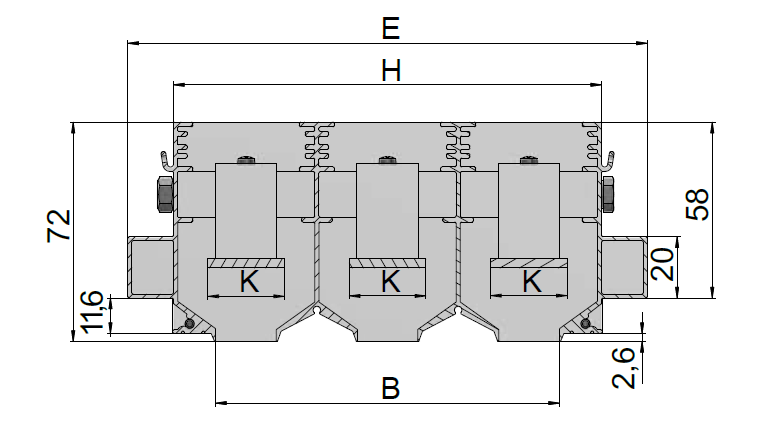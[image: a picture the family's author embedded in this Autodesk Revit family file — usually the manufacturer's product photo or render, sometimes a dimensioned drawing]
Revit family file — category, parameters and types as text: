
# Revit family: GR_Адаптер линейный_Муфта(n)_TL-КСД_R21
name_source: partatom
category: Соединительные детали воздуховодов
units: mm (PartAtom-declared; Revit-internal decimal feet)

## family parameters
Всегда вертикально = Да
Заголовок OmniClass = Metal Ducts
На основе рабочей плоскости = Нет
Номер OmniClass = 23.75.70.14.31
Общий = Нет
При загрузке вырезать с полостями = Нет
Размер круглого соединителя = Использовать диаметр
Тип детали = Мультипорт

## types (10) — shared parameters
ADSK_URL страницы изделия = https://grilles.ru
ADSK_Версия Revit = 2021
ADSK_Единица измерения = шт.
ADSK_Завод-изготовитель = ООО "ВЕНТРЕШЕТКИКОМ"
ADSK_Количество = 1
ADSK_Материал = ADSK_Оцинкованная сталь
ADSK_Наименование = TL-КСД, адаптер вентиляционной решётки радиальный
Изготовитель = ООО "ВЕНТРЕШЕТКИКОМ"
Корпус_Металл_Толщина = 1 мм
Муфта_Металл_Толщина = 1 мм
zero-valued in all types: Отметка по умолчанию

## per-type parameters (varying)
| type | ADSK_Код изделия | Корпус_Высота | Корпус_Длина | Решётка_Высота | Решётка_Положение_Центр | Щёчки_Высота |
| TLS-КСД 20 | 000200 | 182 мм | 158 мм | 116 мм | 79 мм | 13 мм |
| TLS-КСД 30 | 000200 | 182 мм | 168 мм | 126 мм | 84 мм | 13 мм |
| TLS-КСД 40 | 000200 | 222 мм | 178 мм | 136 мм | 89 мм | 13 мм |
| TLS-КСД 50 | 000200 | 222 мм | 188 мм | 146 мм | 94 мм | 13 мм |
| TLS-КСД 60 | 000200 | 272 мм | 198 мм | 156 мм | 99 мм | 13 мм |
| TLS-КСД 70 | 000200 | 272 мм | 208 мм | 166 мм | 104 мм | 13 мм |
| TLM-КСД 40 | 000201 | 222 мм | 178 мм | 136 мм | 89 мм | 24 мм |
| TLM-КСД 50 | 000201 | 222 мм | 188 мм | 146 мм | 94 мм | 24 мм |
| TLL-КСД 60 | 000202 | 272 мм | 238 мм | 196 мм | 119 мм | 26 мм |
| TLL-КСД 70 | 000202 | 272 мм | 248 мм | 206 мм | 124 мм | 26 мм |

note: column(s) folded — value = type name in every type: ADSK_Марка
